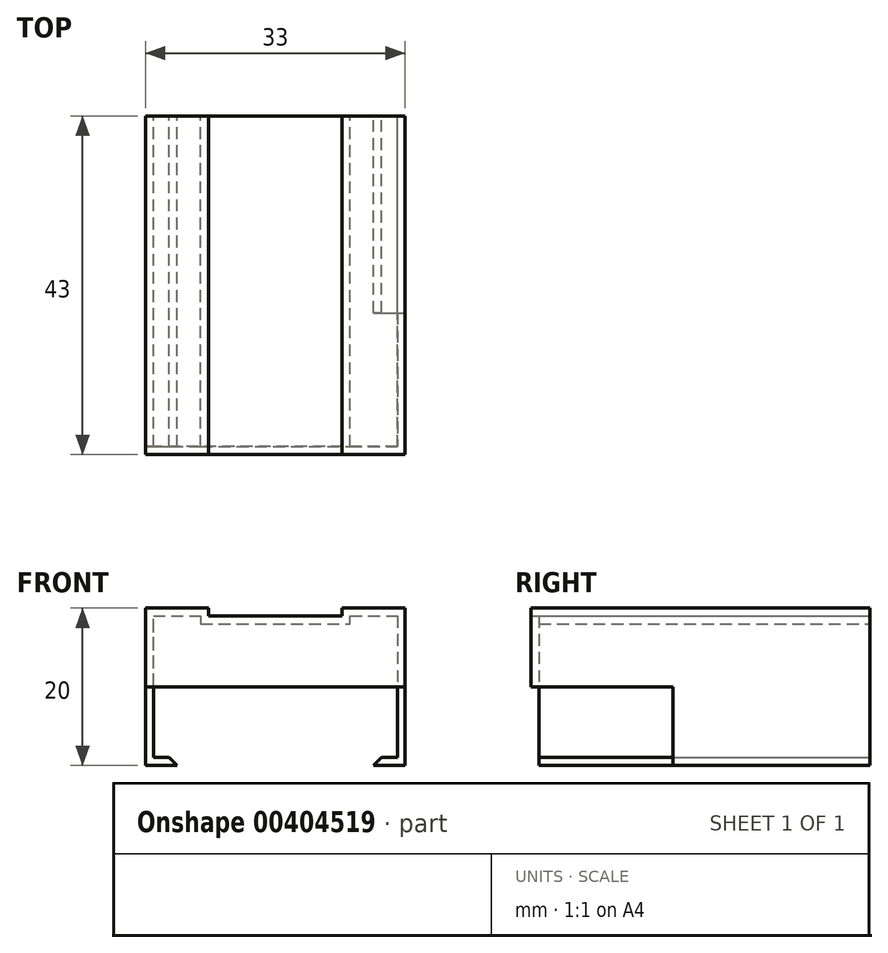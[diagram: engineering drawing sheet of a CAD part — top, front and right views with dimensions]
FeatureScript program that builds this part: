
annotation { "Feature Type Name" : "Feature", "Feature Type Description" : "" }
export const myFeature = defineFeature(function(context is Context, id is Id, definition is map)
    precondition{}
    {
        {
            var Q0;
            Q0=qCreatedBy(makeId("Front.planeOp"),FACE);
            var sketch = newSketch(context, id + "F0", { "sketchPlane" : qUnion([Q0])});
            skLineSegment(sketch, "E0", {"start": v(0, 0) * mm, "end": v(0, 18) * mm});
            skLineSegment(sketch, "E1", {"start": v(0, 18) * mm, "end": v(6, 18) * mm});
            skLineSegment(sketch, "E2", {"start": v(6, 18) * mm, "end": v(6, 17) * mm});
            skLineSegment(sketch, "E3", {"start": v(6, 17) * mm, "end": v(25, 17) * mm});
            skLineSegment(sketch, "E4", {"start": v(25, 17) * mm, "end": v(25, 18) * mm});
            skLineSegment(sketch, "E5", {"start": v(25, 18) * mm, "end": v(31, 18) * mm});
            skLineSegment(sketch, "E6", {"start": v(31, 18) * mm, "end": v(31, 0) * mm});
            skLineSegment(sketch, "E7", {"start": v(0, 0) * mm, "end": v(2, 0) * mm});
            skLineSegment(sketch, "E8", {"start": v(31, 0) * mm, "end": v(29, 0) * mm});
            skLineSegment(sketch, "E9.0", {"start": v(-1, -1) * mm, "end": v(3, -1) * mm});
            skLineSegment(sketch, "E9.1", {"start": v(-1, -1) * mm, "end": v(-1, 19) * mm});
            skLineSegment(sketch, "E9.2", {"start": v(-1, 19) * mm, "end": v(7, 19) * mm});
            skLineSegment(sketch, "E9.3", {"start": v(7, 19) * mm, "end": v(7, 18) * mm});
            skLineSegment(sketch, "E9.4", {"start": v(7, 18) * mm, "end": v(24, 18) * mm});
            skLineSegment(sketch, "E9.5", {"start": v(32, -1) * mm, "end": v(28, -1) * mm});
            skLineSegment(sketch, "E9.6", {"start": v(32, 19) * mm, "end": v(32, -1) * mm});
            skLineSegment(sketch, "E9.7", {"start": v(24, 19) * mm, "end": v(32, 19) * mm});
            skLineSegment(sketch, "E9.8", {"start": v(24, 18) * mm, "end": v(24, 19) * mm});
            skLineSegment(sketch, "E10", {"start": v(28, -1) * mm, "end": v(29, 0) * mm});
            skLineSegment(sketch, "E11", {"start": v(3, -1) * mm, "end": v(2, 0) * mm});
            skSolve(sketch);
        }
        {
            var Q0;
            Q0 = qSketchRegion(id + "F0", true);
            extrude(context, id + "F1", {"entities" : qUnion([Q0]), "depth" : 42 * mm});
        }
        {
            var Q0;
            Q0=makeQuery(id+"F1.opExtrude","SWEPT_FACE",FACE,{"disambiguationData":[OSD([sQuery(id+"F0.wireOp",EDGE,"E9.6")])]});
            var sketch = newSketch(context, id + "F2", { "sketchPlane" : qUnion([Q0])});
            skLineSegment(sketch, "E12", {"start": v(-25, -1) * mm, "end": v(-25, 9) * mm});
            skLineSegment(sketch, "E13", {"start": v(-25, 9) * mm, "end": v(-42, 9) * mm});
            skLineSegment(sketch, "E14", {"start": v(-42, 9) * mm, "end": v(-42, -1) * mm});
            skLineSegment(sketch, "E15", {"start": v(-42, -1) * mm, "end": v(-25, -1) * mm});
            skSolve(sketch);
        }
        {
            var Q0;
            Q0 = qSketchRegion(id + "F2", true);
            extrude(context, id + "F3", {"entities" : qUnion([Q0]), "operationType" : NewBodyOperationType.REMOVE, "oppositeDirection" : true, "depth" : 5 * mm});
        }
        {
            var Q0;
            Q0=makeQuery(id+"F1.opExtrude","CAP_FACE",FACE,{"disambiguationData":[OSD([sQuery(id+"F0.wireOp",EDGE,"E0"),sQuery(id+"F0.wireOp",EDGE,"E1"),sQuery(id+"F0.wireOp",EDGE,"E2"),sQuery(id+"F0.wireOp",EDGE,"E3"),sQuery(id+"F0.wireOp",EDGE,"E4"),sQuery(id+"F0.wireOp",EDGE,"E5"),sQuery(id+"F0.wireOp",EDGE,"E6"),sQuery(id+"F0.wireOp",EDGE,"E7"),sQuery(id+"F0.wireOp",EDGE,"E8"),sQuery(id+"F0.wireOp",EDGE,"E9.0"),sQuery(id+"F0.wireOp",EDGE,"E9.1"),sQuery(id+"F0.wireOp",EDGE,"E9.2"),sQuery(id+"F0.wireOp",EDGE,"E9.3"),sQuery(id+"F0.wireOp",EDGE,"E9.4"),sQuery(id+"F0.wireOp",EDGE,"E9.5"),sQuery(id+"F0.wireOp",EDGE,"E9.6"),sQuery(id+"F0.wireOp",EDGE,"E9.7"),sQuery(id+"F0.wireOp",EDGE,"E9.8"),sQuery(id+"F0.wireOp",EDGE,"E10"),sQuery(id+"F0.wireOp",EDGE,"E11")])],"isStart":false});
            var sketch = newSketch(context, id + "F4", { "sketchPlane" : qUnion([Q0])});
            skLineSegment(sketch, "E16.bottom", {"start": v(32, 9) * mm, "end": v(-1, 9) * mm});
            skLineSegment(sketch, "E16.top", {"start": v(32, 19) * mm, "end": v(24, 19) * mm});
            skLineSegment(sketch, "E16.left", {"start": v(32, 9) * mm, "end": v(32, 19) * mm});
            skLineSegment(sketch, "E16.right", {"start": v(-1, 9) * mm, "end": v(-1, 19) * mm});
            skLineSegment(sketch, "E17.0", {"start": v(7, 18) * mm, "end": v(24, 18) * mm});
            skLineSegment(sketch, "E18.0", {"start": v(7, 19) * mm, "end": v(7, 18) * mm});
            skLineSegment(sketch, "E19.0", {"start": v(24, 18) * mm, "end": v(24, 19) * mm});
            skLineSegment(sketch, "E20.trimOffspring", {"start": v(7, 19) * mm, "end": v(-1, 19) * mm});
            skSolve(sketch);
        }
        {
            var Q0;
            Q0 = qSketchRegion(id + "F4", true);
            extrude(context, id + "F5", {"entities" : qUnion([Q0]), "operationType" : NewBodyOperationType.ADD, "depth" : 1 * mm});
        }
    });
